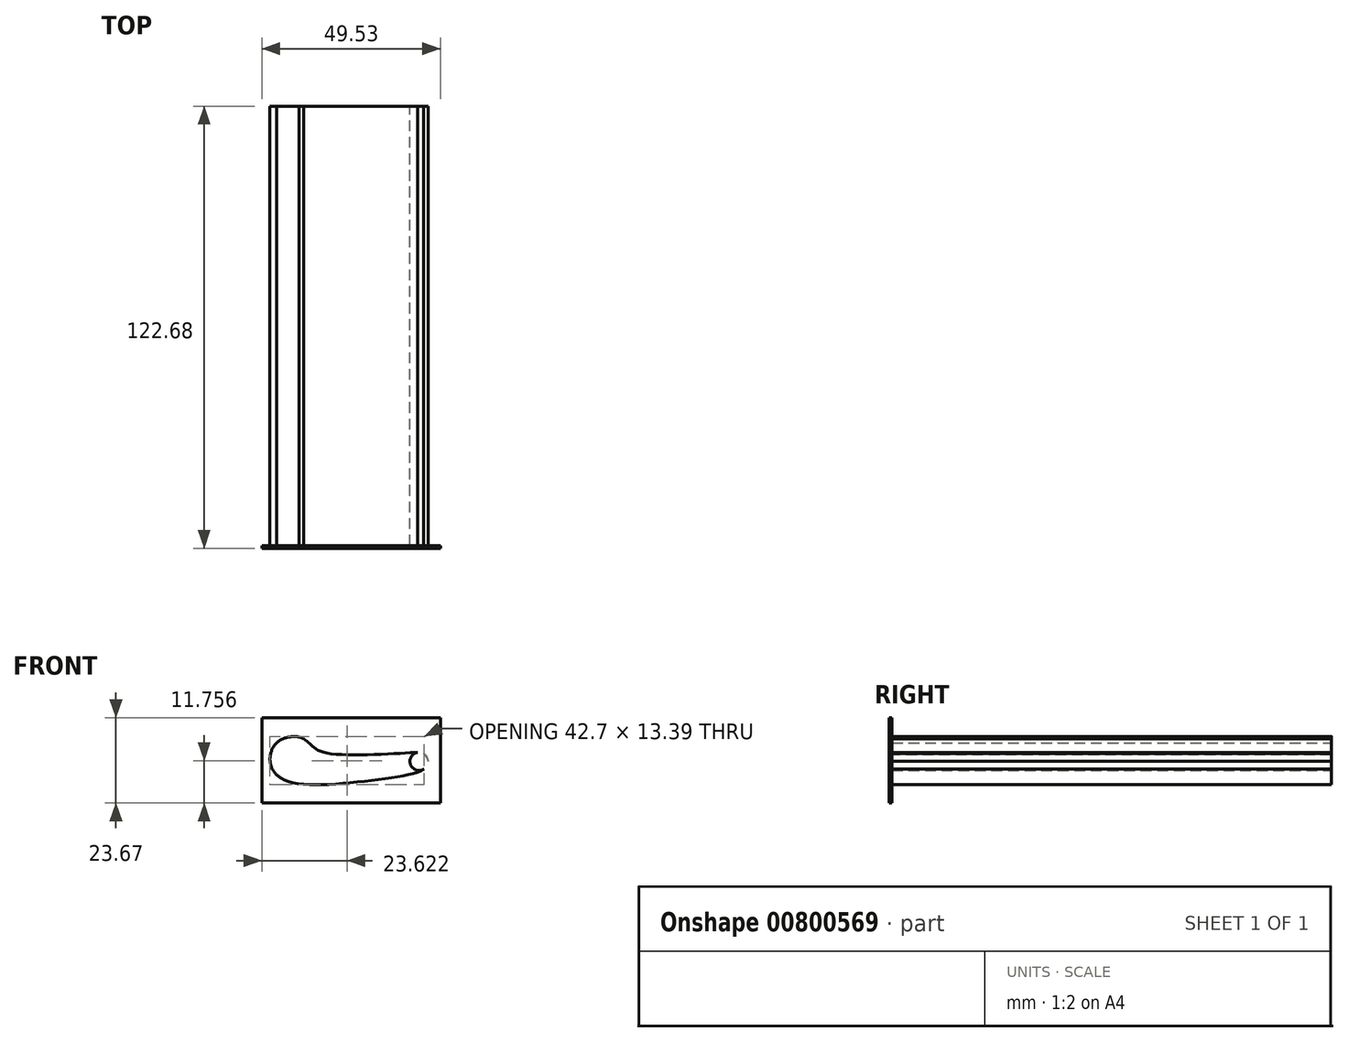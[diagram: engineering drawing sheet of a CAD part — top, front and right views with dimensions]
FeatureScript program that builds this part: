
annotation { "Feature Type Name" : "Feature", "Feature Type Description" : "" }
export const myFeature = defineFeature(function(context is Context, id is Id, definition is map)
    precondition{}
    {
        {
            var Q0;
            Q0=qCreatedBy(makeId("Front.planeOp"),FACE);
            var sketch = newSketch(context, id + "F0", { "sketchPlane" : qUnion([Q0])});
            skCircle(sketch, "E0", {"center": v(-49.76, 25.65) * mm, "radius": 6.35 * mm});
            skCircle(sketch, "E1", {"center": v(-14.75, 24.99) * mm, "radius": 2.54 * mm});
            skFitSpline(sketch, "E2", {"points": [v(-13.4, 22.83) * mm, v(-29.23, 19.58) * mm, v(-51.05, 19.44) * mm, v(-55.95, 24.23) * mm, v(-54.28, 30.11) * mm, v(-48.03, 31.76) * mm, v(-44.8, 29.62) * mm, v(-39.21, 27.13) * mm, v(-14.55, 27.52) * mm, v(-13.55, 27.23) * mm, v(-12.21, 24.99) * mm, v(-13.4, 22.83) * mm]});
            skSolve(sketch);
        }
        {
            var Q0;
            {var subQ0=sQuery(id+"F0.wireOp",EDGE,"E2");var subQ1=sQuery(id+"F0.wireOp",EDGE,"E0");var subQ2=makeQuery(id+"F0.imprint","INTERSECT",VERTEX,{"disambiguationData":[OD(1.0)],"derivedFrom":[subQ1,subQ0]});Q0=makeQuery(id+"F0.imprint","IMPRINT",FACE,{"disambiguationData":[TD([[makeQuery(id+"F0.imprint","IMPRINT",EDGE,{"disambiguationData":[TD([[subQ2,1.0]])],"derivedFrom":subQ1}),-1.0]])]});}
            var Q1;
            {var subQ0=sQuery(id+"F0.wireOp",EDGE,"E2");var subQ1=sQuery(id+"F0.wireOp",EDGE,"E0");var subQ7=makeQuery(id+"F0.imprint","INTERSECT",VERTEX,{"disambiguationData":[OD(0.0)],"derivedFrom":[subQ1,subQ0]});Q1=makeQuery(id+"F0.imprint","IMPRINT",FACE,{"disambiguationData":[TD([[makeQuery(id+"F0.imprint","IMPRINT",EDGE,{"disambiguationData":[TD([[subQ7,-1.0]])],"derivedFrom":subQ1}),1.0]])]});}
            var Q2;
            {var subQ0=sQuery(id+"F0.wireOp",EDGE,"E2");var subQ1=sQuery(id+"F0.wireOp",EDGE,"E1");var subQ4=makeQuery(id+"F0.imprint","INTERSECT",VERTEX,{"disambiguationData":[OD(0.0)],"derivedFrom":[subQ1,subQ0]});Q2=makeQuery(id+"F0.imprint","IMPRINT",FACE,{"disambiguationData":[TD([[makeQuery(id+"F0.imprint","IMPRINT",EDGE,{"disambiguationData":[TD([[subQ4,-1.0]])],"derivedFrom":subQ1}),1.0]])]});}
            extrude(context, id + "F1", {"entities" : qUnion([Q0, Q1, Q2]), "depth" : 63.5 * mm, "offsetDistance" : 25.4 * mm, "hasSecondDirection" : true, "secondDirectionOppositeDirection" : true, "secondDirectionDepth" : 58.42 * mm});
        }
        {
            var Q0;
            Q0=makeQuery(id+"F1.opExtrude","CAP_FACE",FACE,{"disambiguationData":[OSD([sQuery(id+"F0.wireOp",EDGE,"E0"),sQuery(id+"F0.wireOp",EDGE,"E1"),sQuery(id+"F0.wireOp",EDGE,"E2")])],"isStart":false});
            var sketch = newSketch(context, id + "F2", { "sketchPlane" : qUnion([Q0])});
            skLineSegment(sketch, "E3.bottom", {"start": v(-58.38, 13.45) * mm, "end": v(-8.85, 13.45) * mm});
            skLineSegment(sketch, "E3.top", {"start": v(-58.38, 37.12) * mm, "end": v(-8.85, 37.12) * mm});
            skLineSegment(sketch, "E3.left", {"start": v(-58.38, 13.45) * mm, "end": v(-58.38, 37.12) * mm});
            skLineSegment(sketch, "E3.right", {"start": v(-8.85, 13.45) * mm, "end": v(-8.85, 37.12) * mm});
            skSolve(sketch);
        }
        {
            var Q0;
            Q0=makeQuery(id+"F2.imprint","IMPRINT",FACE,{"disambiguationData":[TD([[makeQuery(id+"F2.imprint","IMPRINT",EDGE,{"derivedFrom":sQuery(id+"F2.wireOp",EDGE,"E3.bottom")}),1.0]])]});
            var Q1;
            Q1=sQuery(id+"F2.wireOp",EDGE,"E3.left");
            extrude(context, id + "F3", {"entities" : qUnion([Q0]), "operationType" : NewBodyOperationType.ADD, "surfaceEntities" : qUnion([Q1]), "depth" : 0.76 * mm, "offsetDistance" : 25.4 * mm});
        }
    });
